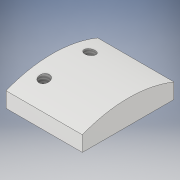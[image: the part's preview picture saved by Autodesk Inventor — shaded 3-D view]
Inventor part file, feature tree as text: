
AUTODESK INVENTOR PART (.ipt)
format: ipt  version: 2017 (Build 210142000, 142)  size: 116,224 bytes
history: native  units: in
note: dims shown in document units (in); Inventor stores cm internally (conversion verified against a paired STEP export)
features: sketch x2, extrude x1, hole x1, projected_geometry x1
ambient origin geometry x8: Origin, YZ Plane, XZ Plane, XY Plane, X Axis, Y Axis, Z Axis, Center Point
bodies: Solid1 (feature_tree)
feature tree (5):
  extrude  "Extrusion1"  Depth=0.125in
  hole  "Hole1"  [1 undecoded]
  sketch  "Sketch1"  dims[d0=0.75in d4=0.125in]
  sketch  "Sketch2"  dims[d6=1.0in d7=0.75in d8=0.625in d9=0.0in d10=0.625in d13=0.375in d14=0.75in d15=0.1875in d16=0.085in d17=0.224in d18=0.375in d19=0.25in d20=0.5635in d21=0.25in d22=0.8108in d23=0.125in d24=0.125in d25=0.125in]
  projected_geometry  "Projected Loop1"
note: 1 required parameter value undecoded (feature->parameter linkage not recoverable at this tier; creation-order binding heuristic only, values carry confidence <= 0.55)
